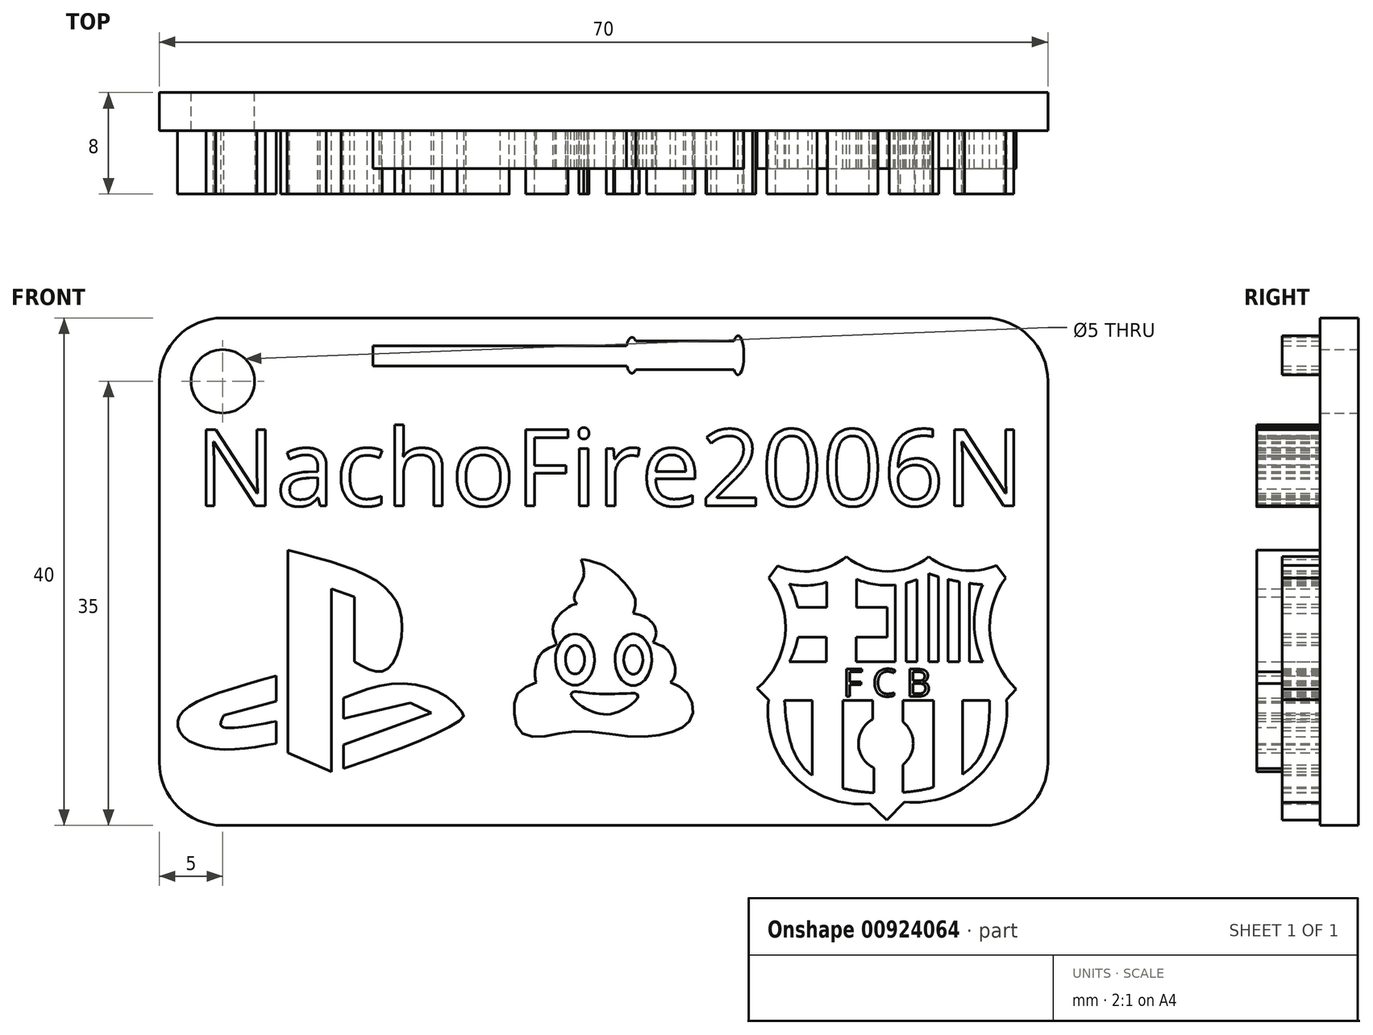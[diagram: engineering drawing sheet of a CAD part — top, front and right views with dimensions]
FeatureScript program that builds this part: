
annotation { "Feature Type Name" : "Feature", "Feature Type Description" : "" }
export const myFeature = defineFeature(function(context is Context, id is Id, definition is map)
    precondition{}
    {
        {
            var Q0;
            Q0=qCreatedBy(makeId("Front.planeOp"),FACE);
            var sketch = newSketch(context, id + "F0", { "sketchPlane" : qUnion([Q0])});
            skLineSegment(sketch, "E0.bottom", {"start": v(-5, 0) * mm, "end": v(-65, 0) * mm});
            skLineSegment(sketch, "E0.top", {"start": v(-5, 40) * mm, "end": v(-65, 40) * mm});
            skLineSegment(sketch, "E0.left", {"start": v(0, 5) * mm, "end": v(0, 35) * mm});
            skLineSegment(sketch, "E0.right", {"start": v(-70, 5) * mm, "end": v(-70, 35) * mm});
            skPoint(sketch, "E1.visualSharp", {"position": v(-70, 40) * mm});
            skArc(sketch, "E1.filletArc", {"start": v(-65, 40) * mm, "mid": v(-68.54, 38.54) * mm, "end": v(-70, 35) * mm});
            skPoint(sketch, "E2.visualSharp", {"position": v(-70, 0) * mm});
            skArc(sketch, "E2.filletArc", {"start": v(-70, 5) * mm, "mid": v(-68.54, 1.46) * mm, "end": v(-65, 0) * mm});
            skPoint(sketch, "E3.visualSharp", {"position": v(0, 40) * mm});
            skArc(sketch, "E3.filletArc", {"start": v(0, 35) * mm, "mid": v(-1.46, 38.54) * mm, "end": v(-5, 40) * mm});
            skPoint(sketch, "E4.visualSharp", {"position": v(0, 0) * mm});
            skArc(sketch, "E4.filletArc", {"start": v(-5, 0) * mm, "mid": v(-1.46, 1.46) * mm, "end": v(0, 5) * mm});
            skCircle(sketch, "E5", {"center": v(-65, 35) * mm, "radius": 2.5 * mm});
            skSolve(sketch);
        }
        {
            var Q0;
            Q0 = qSketchRegion(id + "F0", true);
            extrude(context, id + "F1", {"entities" : qUnion([Q0]), "depth" : 3 * mm, "offsetDistance" : 25 * mm});
        }
        {
            var Q0;
            Q0=makeQuery(id+"F1.opExtrude","CAP_FACE",FACE,{"disambiguationData":[OSD([sQuery(id+"F0.wireOp",EDGE,"E0.bottom"),sQuery(id+"F0.wireOp",EDGE,"E0.top"),sQuery(id+"F0.wireOp",EDGE,"E0.left"),sQuery(id+"F0.wireOp",EDGE,"E0.right"),sQuery(id+"F0.wireOp",EDGE,"E1.filletArc"),sQuery(id+"F0.wireOp",EDGE,"E2.filletArc"),sQuery(id+"F0.wireOp",EDGE,"E3.filletArc"),sQuery(id+"F0.wireOp",EDGE,"E4.filletArc"),sQuery(id+"F0.wireOp",EDGE,"E5")])],"isStart":false});
            var sketch = newSketch(context, id + "F2", { "sketchPlane" : qUnion([Q0])});
            skText(sketch, "E6", { "text": "NachoFire2006N", "fontName": "OpenSans-Regular.ttf"});
            skPoint(sketch, "E7.start.orphan", {"position": v(-58.07, 12.98) * mm});
            skPoint(sketch, "E8.start.orphan", {"position": v(-58.07, 12.23) * mm});
            skPoint(sketch, "E9.end.orphan", {"position": v(-55.4, 11.37) * mm});
            skPoint(sketch, "E10.start.orphan", {"position": v(-55.4, 12.32) * mm});
            skPoint(sketch, "E11.2.internal.orphan", {"position": v(-62.68, 9.55) * mm});
            skPoint(sketch, "E11.3.internal.orphan", {"position": v(-59.99, 9.94) * mm});
            skPoint(sketch, "E12.end.orphan", {"position": v(-62.68, 10.23) * mm});
            skPoint(sketch, "E13.end.orphan", {"position": v(-59.99, 10.93) * mm});
            skPoint(sketch, "E14.2.internal.orphan", {"position": v(-51.14, 11.2) * mm});
            skPoint(sketch, "E15.end.orphan", {"position": v(-56.52, 10.05) * mm});
            skPoint(sketch, "E15.start.orphan", {"position": v(-56.52, 11.2) * mm});
            skPoint(sketch, "E16.start.orphan", {"position": v(-56.52, 8.65) * mm});
            skLineSegment(sketch, "E17", {"start": v(-59.87, 21.7) * mm, "end": v(-59.87, 5.73) * mm});
            skLineSegment(sketch, "E18", {"start": v(-59.87, 5.73) * mm, "end": v(-56.44, 4.25) * mm});
            skLineSegment(sketch, "E19", {"start": v(-56.44, 4.25) * mm, "end": v(-56.44, 18.66) * mm});
            skLineSegment(sketch, "E20", {"start": v(-56.44, 18.66) * mm, "end": v(-54.63, 18) * mm});
            skLineSegment(sketch, "E21", {"start": v(-54.63, 18) * mm, "end": v(-54.63, 12.9) * mm});
            skFitSpline(sketch, "E22", {"points": [v(-59.87, 21.7) * mm, v(-52.24, 18.78) * mm, v(-50.89, 15.3) * mm, v(-52.24, 12.2) * mm, v(-54.63, 12.9) * mm], "startDerivative": vector(26.14, -6.65) * mm, "endDerivative": vector(-13.47, 7.9) * mm});
            skLineSegment(sketch, "E23", {"start": v(-55.5, 10.05) * mm, "end": v(-55.5, 8.43) * mm});
            skLineSegment(sketch, "E24", {"start": v(-55.5, 6.38) * mm, "end": v(-55.5, 4.5) * mm});
            skLineSegment(sketch, "E25", {"start": v(-55.5, 6.38) * mm, "end": v(-48.55, 8.86) * mm});
            skLineSegment(sketch, "E26", {"start": v(-48.55, 8.86) * mm, "end": v(-50.22, 9.67) * mm});
            skLineSegment(sketch, "E27", {"start": v(-50.22, 9.67) * mm, "end": v(-55.5, 8.43) * mm});
            skPoint(sketch, "E28.5.internal.snap0", {"position": v(-52.02, 7.62) * mm});
            skFitSpline(sketch, "E28", {"points": [v(-55.5, 10.05) * mm, v(-51.14, 11.2) * mm, v(-47.51, 10.24) * mm, v(-46.23, 9.03) * mm, v(-46.06, 8.54) * mm, v(-52.02, 5.69) * mm, v(-55.5, 4.5) * mm], "startDerivative": vector(21.53, 8.3) * mm, "endDerivative": vector(-15.4, -4.87) * mm});
            skLineSegment(sketch, "E29", {"start": v(-60.79, 11.8) * mm, "end": v(-60.79, 9.8) * mm});
            skLineSegment(sketch, "E30", {"start": v(-60.79, 8.2) * mm, "end": v(-60.79, 6.46) * mm});
            skLineSegment(sketch, "E31", {"start": v(-60.79, 9.8) * mm, "end": v(-64.91, 8.67) * mm});
            skFitSpline(sketch, "E32", {"points": [v(-64.91, 8.67) * mm, v(-65.16, 8.08) * mm, v(-65.02, 7.76) * mm, v(-60.79, 8.2) * mm], "startDerivative": vector(-1.43, -2.66) * mm, "endDerivative": vector(9.4, 1.72) * mm});
            skFitSpline(sketch, "E33", {"points": [v(-60.79, 6.46) * mm, v(-65.2, 6.01) * mm, v(-68.05, 6.95) * mm, v(-68.56, 8.16) * mm, v(-67.6, 9.4) * mm, v(-60.79, 11.8) * mm], "startDerivative": vector(-19.03, -3.5) * mm, "endDerivative": vector(27.45, 7.68) * mm});
            const initialGuessF2  = {"E6": [-0.06715, 0.0252, 1, 0, 0.00604]};
            skSetInitialGuess(sketch, initialGuessF2);
            skSolve(sketch);
        }
        {
            var Q0;
            Q0 = qSketchRegion(id + "F2", true);
            extrude(context, id + "F3", {"entities" : qUnion([Q0]), "operationType" : NewBodyOperationType.ADD, "depth" : 5 * mm, "offsetDistance" : 25 * mm});
        }
        {
            var Q0;
            {var subQ0=sQuery(id+"F0.wireOp",EDGE,"E0.left");var subQ1=sQuery(id+"F0.wireOp",EDGE,"E5");var subQ2=sQuery(id+"F0.wireOp",EDGE,"E4.filletArc");var subQ3=sQuery(id+"F0.wireOp",EDGE,"E3.filletArc");var subQ4=sQuery(id+"F0.wireOp",EDGE,"E2.filletArc");var subQ5=sQuery(id+"F0.wireOp",EDGE,"E1.filletArc");var subQ6=sQuery(id+"F0.wireOp",EDGE,"E0.bottom");var subQ7=sQuery(id+"F0.wireOp",EDGE,"E0.right");var subQ8=sQuery(id+"F0.wireOp",EDGE,"E0.top");Q0=makeQuery(id+"F3.boolean.opBoolean","SPLIT",FACE,{"disambiguationData":[TD([makeQuery(id+"F1.opExtrude","SWEPT_FACE",FACE,{"disambiguationData":[OSD([subQ6])]})])],"derivedFrom":makeQuery(id+"F1.opExtrude","CAP_FACE",FACE,{"disambiguationData":[OSD([subQ6,subQ8,subQ0,subQ7,subQ5,subQ4,subQ3,subQ2,subQ1])],"isStart":false})});}
            var sketch = newSketch(context, id + "F4", { "sketchPlane" : qUnion([Q0])});
            skCircle(sketch, "E34", {"center": v(-12.76, 6.47) * mm, "radius": 2.16 * mm});
            skLineSegment(sketch, "E35", {"start": v(-20.76, 9.86) * mm, "end": v(-4.58, 9.86) * mm});
            skLineSegment(sketch, "E36", {"start": v(-20.37, 12.9) * mm, "end": v(-5.13, 12.9) * mm});
            skFitSpline(sketch, "E37", {"points": [v(-20.76, 9.86) * mm, v(-18.77, 4.11) * mm, v(-9.71, 2.84) * mm, v(-5.3, 5.55) * mm, v(-4.58, 9.86) * mm], "startDerivative": vector(2.2, -26.55) * mm, "endDerivative": vector(0.34, 21.86) * mm});
            skLineSegment(sketch, "E38", {"start": v(-18.55, 9.86) * mm, "end": v(-18.55, 3.95) * mm});
            skLineSegment(sketch, "E39", {"start": v(-16.15, 2.93) * mm, "end": v(-16.15, 9.86) * mm});
            skLineSegment(sketch, "E40", {"start": v(-13.8, 9.86) * mm, "end": v(-13.8, 8.37) * mm});
            skLineSegment(sketch, "E41", {"start": v(-13.7, 4.53) * mm, "end": v(-13.7, 2.58) * mm});
            skLineSegment(sketch, "E42", {"start": v(-11.42, 9.86) * mm, "end": v(-11.42, 8.16) * mm});
            skLineSegment(sketch, "E43", {"start": v(-11.43, 4.77) * mm, "end": v(-11.43, 2.6) * mm});
            skLineSegment(sketch, "E44", {"start": v(-9, 3.01) * mm, "end": v(-9, 9.86) * mm});
            skLineSegment(sketch, "E45", {"start": v(-6.73, 9.86) * mm, "end": v(-6.73, 4.01) * mm});
            skArc(sketch, "E46", {"start": v(-20.37, 12.9) * mm, "mid": v(-19.59, 15.96) * mm, "end": v(-20.37, 19.02) * mm});
            skArc(sketch, "E47", {"start": v(-5.13, 18.98) * mm, "mid": v(-5.8, 15.93) * mm, "end": v(-5.13, 12.9) * mm});
            skArc(sketch, "E48", {"start": v(-9.38, 19.85) * mm, "mid": v(-7.29, 19.27) * mm, "end": v(-5.13, 18.98) * mm});
            skArc(sketch, "E49", {"start": v(-15.95, 19.85) * mm, "mid": v(-12.67, 18.92) * mm, "end": v(-9.38, 19.85) * mm});
            skArc(sketch, "E50", {"start": v(-20.37, 19.02) * mm, "mid": v(-18.08, 19.01) * mm, "end": v(-15.95, 19.85) * mm});
            skLineSegment(sketch, "E51", {"start": v(-12.67, 18.92) * mm, "end": v(-12.67, 12.9) * mm});
            skLineSegment(sketch, "E52", {"start": v(-12.02, 12.9) * mm, "end": v(-12.02, 18.96) * mm});
            skLineSegment(sketch, "E53", {"start": v(-11.17, 19.1) * mm, "end": v(-11.17, 12.9) * mm});
            skLineSegment(sketch, "E54", {"start": v(-10.31, 19.38) * mm, "end": v(-10.31, 12.9) * mm});
            skLineSegment(sketch, "E55", {"start": v(-9.38, 19.85) * mm, "end": v(-9.38, 12.9) * mm});
            skLineSegment(sketch, "E56", {"start": v(-8.62, 19.6) * mm, "end": v(-8.62, 12.9) * mm});
            skLineSegment(sketch, "E57", {"start": v(-7.87, 19.4) * mm, "end": v(-7.87, 12.9) * mm});
            skLineSegment(sketch, "E58", {"start": v(-6.96, 19.2) * mm, "end": v(-6.96, 12.9) * mm});
            skLineSegment(sketch, "E59", {"start": v(-6.2, 19.09) * mm, "end": v(-6.2, 12.9) * mm});
            skLineSegment(sketch, "E60", {"start": v(-15.08, 19.4) * mm, "end": v(-15.08, 17.2) * mm});
            skLineSegment(sketch, "E61", {"start": v(-15.08, 17.2) * mm, "end": v(-12.67, 17.2) * mm});
            skLineSegment(sketch, "E62", {"start": v(-12.67, 14.85) * mm, "end": v(-15.1, 14.85) * mm});
            skLineSegment(sketch, "E63", {"start": v(-15.1, 14.85) * mm, "end": v(-15.1, 12.9) * mm});
            skLineSegment(sketch, "E64", {"start": v(-17.42, 19.18) * mm, "end": v(-17.42, 17.2) * mm});
            skLineSegment(sketch, "E65", {"start": v(-17.42, 17.2) * mm, "end": v(-19.7, 17.2) * mm});
            skLineSegment(sketch, "E66", {"start": v(-17.45, 14.85) * mm, "end": v(-19.68, 14.85) * mm});
            skLineSegment(sketch, "E67", {"start": v(-17.45, 14.85) * mm, "end": v(-17.45, 12.9) * mm});
            skText(sketch, "E68", { "text": "F C B", "fontName": "OpenSans-Regular.ttf"});
            skLineSegment(sketch, "E69", {"start": v(-4.05, 20.5) * mm, "end": v(-3.33, 19.52) * mm});
            skLineSegment(sketch, "E70", {"start": v(-22, 19.52) * mm, "end": v(-21.28, 20.47) * mm});
            skLineSegment(sketch, "E71", {"start": v(-22.91, 10.8) * mm, "end": v(-22, 9.88) * mm});
            skLineSegment(sketch, "E72", {"start": v(-2.5, 10.76) * mm, "end": v(-3.26, 9.92) * mm});
            skPoint(sketch, "E72.startSnap0", {"position": v(-1.83, 10.76) * mm});
            skLineSegment(sketch, "E73", {"start": v(-14.05, 1.73) * mm, "end": v(-12.68, 0.4) * mm});
            skLineSegment(sketch, "E74", {"start": v(-12.68, 0.4) * mm, "end": v(-11.3, 1.85) * mm});
            skArc(sketch, "E75", {"start": v(-22, 9.88) * mm, "mid": v(-19.99, 3.89) * mm, "end": v(-14.05, 1.73) * mm});
            skArc(sketch, "E76", {"start": v(-11.3, 1.85) * mm, "mid": v(-5.36, 3.98) * mm, "end": v(-3.26, 9.92) * mm});
            skArc(sketch, "E77", {"start": v(-3.33, 19.52) * mm, "mid": v(-4.55, 14.98) * mm, "end": v(-2.5, 10.76) * mm});
            skPoint(sketch, "E78", {"position": v(-15.87, 21.19) * mm});
            skPoint(sketch, "E79", {"position": v(-9.38, 21.19) * mm});
            skArc(sketch, "E80", {"start": v(-22.91, 10.8) * mm, "mid": v(-20.7, 14.97) * mm, "end": v(-22, 19.52) * mm});
            skArc(sketch, "E81", {"start": v(-21.28, 20.47) * mm, "mid": v(-18.47, 20.06) * mm, "end": v(-15.87, 21.19) * mm});
            skArc(sketch, "E82", {"start": v(-15.87, 21.19) * mm, "mid": v(-12.63, 20.02) * mm, "end": v(-9.38, 21.19) * mm});
            skArc(sketch, "E83", {"start": v(-9.38, 21.19) * mm, "mid": v(-6.81, 20.11) * mm, "end": v(-4.05, 20.5) * mm});
            skFitSpline(sketch, "E84", {"points": [v(-12.76, 6.47) * mm, v(-13, 5.98) * mm, v(-13.7, 5.93) * mm, v(-14.18, 6.95) * mm, v(-13.92, 8.3) * mm], "startDerivative": vector(-0.68, -2.87) * mm, "endDerivative": vector(1.41, 4.28) * mm});
            skFitSpline(sketch, "E85", {"points": [v(-12.76, 6.47) * mm, v(-13, 7.36) * mm, v(-12.35, 7.64) * mm, v(-10.62, 6.7) * mm], "startDerivative": vector(-1.62, 3.35) * mm, "endDerivative": vector(4.18, -3.07) * mm});
            skArc(sketch, "E86", {"start": v(-12.76, 8.63) * mm, "mid": v(-12.98, 8.1) * mm, "end": v(-12.68, 7.62) * mm});
            skFitSpline(sketch, "E87", {"points": [v(-12.76, 6.47) * mm, v(-12, 6.47) * mm, v(-11.62, 5.83) * mm, v(-12.93, 4.77) * mm, v(-13.96, 4.68) * mm], "startDerivative": vector(3.7, 0.74) * mm, "endDerivative": vector(-3.72, 0.32) * mm});
            skArc(sketch, "E88", {"start": v(-10.8, 5.6) * mm, "mid": v(-11.15, 5.91) * mm, "end": v(-11.62, 5.83) * mm});
            skArc(sketch, "E89", {"start": v(-14.68, 5.48) * mm, "mid": v(-14.11, 5.54) * mm, "end": v(-13.7, 5.93) * mm});
            const initialGuessF4  = {"E68": [-0.01616, 0.01018, 1, 0, 0.00216]};
            skSetInitialGuess(sketch, initialGuessF4);
            skSolve(sketch);
        }
        {
            var Q0;
            Q0 = qSketchRegion(id + "F4", true);
            var Q1;
            {var subQ4=sQuery(id+"F4.wireOp",EDGE,"E60");Q1=makeQuery(id+"F4.imprint","IMPRINT",FACE,{"disambiguationData":[TD([[makeQuery(id+"F4.imprint","IMPRINT",EDGE,{"derivedFrom":subQ4}),-1.0]])]});}
            var Q2;
            {var subQ0=sQuery(id+"F4.wireOp",EDGE,"E58");Q2=makeQuery(id+"F4.imprint","IMPRINT",FACE,{"disambiguationData":[TD([[makeQuery(id+"F4.imprint","IMPRINT",EDGE,{"derivedFrom":subQ0}),1.0]])]});}
            var Q3;
            {var subQ0=sQuery(id+"F4.wireOp",EDGE,"E56");Q3=makeQuery(id+"F4.imprint","IMPRINT",FACE,{"disambiguationData":[TD([[makeQuery(id+"F4.imprint","IMPRINT",EDGE,{"derivedFrom":subQ0}),1.0]])]});}
            var Q4;
            {var subQ0=sQuery(id+"F4.wireOp",EDGE,"E54");Q4=makeQuery(id+"F4.imprint","IMPRINT",FACE,{"disambiguationData":[TD([[makeQuery(id+"F4.imprint","IMPRINT",EDGE,{"derivedFrom":subQ0}),1.0]])]});}
            var Q5;
            {var subQ0=sQuery(id+"F4.wireOp",EDGE,"E52");Q5=makeQuery(id+"F4.imprint","IMPRINT",FACE,{"disambiguationData":[TD([[makeQuery(id+"F4.imprint","IMPRINT",EDGE,{"derivedFrom":subQ0}),-1.0]])]});}
            var Q6;
            {var subQ0=sQuery(id+"F4.wireOp",EDGE,"E34");var subQ1=makeQuery(id+"F4.imprint","INTERSECT",VERTEX,{"derivedFrom":[subQ0,sQuery(id+"F4.wireOp",EDGE,"E40")]});Q6=makeQuery(id+"F4.imprint","IMPRINT",FACE,{"disambiguationData":[TD([[makeQuery(id+"F4.imprint","IMPRINT",EDGE,{"disambiguationData":[TD([[subQ1,1.0]])],"derivedFrom":subQ0}),1.0]])]});}
            var Q7;
            {var subQ0=sQuery(id+"F4.wireOp",EDGE,"E40");Q7=makeQuery(id+"F4.imprint","IMPRINT",FACE,{"disambiguationData":[TD([[makeQuery(id+"F4.imprint","IMPRINT",EDGE,{"derivedFrom":subQ0}),1.0]])]});}
            var Q8;
            {var subQ0=sQuery(id+"F4.wireOp",EDGE,"E38");Q8=makeQuery(id+"F4.imprint","IMPRINT",FACE,{"disambiguationData":[TD([[makeQuery(id+"F4.imprint","IMPRINT",EDGE,{"derivedFrom":subQ0}),1.0]])]});}
            var Q9;
            {var subQ0=sQuery(id+"F4.wireOp",EDGE,"E41");Q9=makeQuery(id+"F4.imprint","IMPRINT",FACE,{"disambiguationData":[TD([[makeQuery(id+"F4.imprint","IMPRINT",EDGE,{"derivedFrom":subQ0}),1.0]])]});}
            var Q10;
            {var subQ0=sQuery(id+"F4.wireOp",EDGE,"E44");Q10=makeQuery(id+"F4.imprint","IMPRINT",FACE,{"disambiguationData":[TD([[makeQuery(id+"F4.imprint","IMPRINT",EDGE,{"derivedFrom":subQ0}),-1.0]])]});}
            var Q11;
            Q11=makeQuery(id+"F4.imprint","IMPRINT",FACE,{"disambiguationData":[TD([[makeQuery(id+"F4.imprint","IMPRINT",EDGE,{"derivedFrom":sQuery(id+"F4.wireOp",EDGE,"E68.sketch_text.stroke-36")}),1.0]])]});
            var Q12;
            Q12=makeQuery(id+"F4.imprint","IMPRINT",FACE,{"disambiguationData":[TD([[makeQuery(id+"F4.imprint","IMPRINT",EDGE,{"derivedFrom":sQuery(id+"F4.wireOp",EDGE,"E68.sketch_text.stroke-43")}),1.0]])]});
            var Q13;
            {var subQ3=sQuery(id+"F4.wireOp",EDGE,"E88");Q13=makeQuery(id+"F4.imprint","IMPRINT",FACE,{"disambiguationData":[TD([[makeQuery(id+"F4.imprint","IMPRINT",EDGE,{"derivedFrom":subQ3}),-1.0]])]});}
            var Q14;
            {var subQ3=sQuery(id+"F4.wireOp",EDGE,"E88");Q14=makeQuery(id+"F4.imprint","IMPRINT",FACE,{"disambiguationData":[TD([[makeQuery(id+"F4.imprint","IMPRINT",EDGE,{"derivedFrom":subQ3}),1.0]])]});}
            var Q15;
            {var subQ3=sQuery(id+"F4.wireOp",EDGE,"E89");Q15=makeQuery(id+"F4.imprint","IMPRINT",FACE,{"disambiguationData":[TD([[makeQuery(id+"F4.imprint","IMPRINT",EDGE,{"derivedFrom":subQ3}),1.0]])]});}
            var Q16;
            {var subQ6=sQuery(id+"F4.wireOp",EDGE,"E89");Q16=makeQuery(id+"F4.imprint","IMPRINT",FACE,{"disambiguationData":[TD([[makeQuery(id+"F4.imprint","IMPRINT",EDGE,{"derivedFrom":subQ6}),-1.0]])]});}
            var Q17;
            {var subQ4=sQuery(id+"F4.wireOp",EDGE,"E86");Q17=makeQuery(id+"F4.imprint","IMPRINT",FACE,{"disambiguationData":[TD([[makeQuery(id+"F4.imprint","IMPRINT",EDGE,{"derivedFrom":subQ4}),1.0]])]});}
            extrude(context, id + "F5", {"entities" : qUnion([Q0, Q1, Q2, Q3, Q4, Q5, Q6, Q7, Q8, Q9, Q10, Q11, Q12, Q13, Q14, Q15, Q16, Q17]), "operationType" : NewBodyOperationType.ADD, "depth" : 3 * mm, "offsetDistance" : 25 * mm});
        }
        {
            var Q0;
            {var subQ94=sQuery(id+"F0.wireOp",EDGE,"E0.left");var subQ100=sQuery(id+"F0.wireOp",EDGE,"E5");var subQ107=sQuery(id+"F0.wireOp",EDGE,"E4.filletArc");var subQ114=sQuery(id+"F0.wireOp",EDGE,"E3.filletArc");var subQ120=sQuery(id+"F0.wireOp",EDGE,"E2.filletArc");var subQ128=sQuery(id+"F0.wireOp",EDGE,"E1.filletArc");var subQ131=sQuery(id+"F0.wireOp",EDGE,"E0.bottom");var subQ132=makeQuery(id+"F1.opExtrude","SWEPT_FACE",FACE,{"disambiguationData":[OSD([subQ131])]});var subQ136=sQuery(id+"F0.wireOp",EDGE,"E0.right");var subQ140=sQuery(id+"F0.wireOp",EDGE,"E0.top");Q0=makeQuery(id+"F5.boolean.opBoolean","SPLIT",FACE,{"disambiguationData":[TD([subQ132])],"derivedFrom":makeQuery(id+"F3.boolean.opBoolean","SPLIT",FACE,{"disambiguationData":[TD([subQ132])],"derivedFrom":makeQuery(id+"F1.opExtrude","CAP_FACE",FACE,{"disambiguationData":[OSD([subQ131,subQ140,subQ94,subQ136,subQ128,subQ120,subQ114,subQ107,subQ100])],"isStart":false})})});}
            var sketch = newSketch(context, id + "F6", { "sketchPlane" : qUnion([Q0])});
            skLineSegment(sketch, "E90", {"start": v(-32.18, 35.9) * mm, "end": v(-24.8, 35.9) * mm});
            skLineSegment(sketch, "E91", {"start": v(-32.18, 38.2) * mm, "end": v(-24.8, 38.2) * mm});
            skEllipse(sketch, "E92", {"center": v(-24.4, 37.05) * mm, "majorRadius": 1.55 * mm, "minorRadius": 0.46 * mm, "majorAxis": v(0, 1)});
            skLineSegment(sketch, "E93", {"start": v(-24.8, 38.2) * mm, "end": v(-24.72, 38.2) * mm});
            skLineSegment(sketch, "E94", {"start": v(-24.8, 35.9) * mm, "end": v(-24.72, 35.9) * mm});
            skEllipse(sketch, "E95", {"center": v(-32.77, 37.05) * mm, "majorRadius": 1.43 * mm, "minorRadius": 0.49 * mm, "majorAxis": v(0, 1)});
            skLineSegment(sketch, "E96", {"start": v(-32.18, 38.2) * mm, "end": v(-32.48, 38.2) * mm});
            skLineSegment(sketch, "E97", {"start": v(-32.18, 35.9) * mm, "end": v(-32.48, 35.9) * mm});
            skLineSegment(sketch, "E98", {"start": v(-33.18, 37.8) * mm, "end": v(-53.18, 37.8) * mm});
            skLineSegment(sketch, "E99", {"start": v(-53.18, 37.8) * mm, "end": v(-53.18, 36.2) * mm});
            skLineSegment(sketch, "E100", {"start": v(-53.18, 36.2) * mm, "end": v(-33.16, 36.2) * mm});
            skSolve(sketch);
        }
        {
            var Q0;
            {var subQ0=sQuery(id+"F6.wireOp",EDGE,"E92");var subQ1=makeQuery(id+"F6.imprint","INTERSECT",VERTEX,{"derivedFrom":[subQ0,sQuery(id+"F6.wireOp",EDGE,"E93")]});Q0=makeQuery(id+"F6.imprint","IMPRINT",FACE,{"disambiguationData":[TD([[makeQuery(id+"F6.imprint","IMPRINT",EDGE,{"disambiguationData":[TD([[subQ1,-1.0]])],"derivedFrom":subQ0}),1.0]])]});}
            var Q1;
            {var subQ0=sQuery(id+"F6.wireOp",EDGE,"E98");Q1=makeQuery(id+"F6.imprint","IMPRINT",FACE,{"disambiguationData":[TD([[makeQuery(id+"F6.imprint","IMPRINT",EDGE,{"derivedFrom":subQ0}),1.0]])]});}
            var Q2;
            {var subQ0=sQuery(id+"F6.wireOp",EDGE,"uE8yDqcb-mppc-h1kh-nOKK-Aj263YFdmIPn");Q2=makeQuery(id+"F6.imprint","IMPRINT",FACE,{"disambiguationData":[TD([[makeQuery(id+"F6.imprint","IMPRINT",EDGE,{"derivedFrom":subQ0}),-1.0]])]});}
            var Q3;
            {var subQ0=sQuery(id+"F6.wireOp",EDGE,"E93");Q3=makeQuery(id+"F6.imprint","IMPRINT",FACE,{"disambiguationData":[TD([[makeQuery(id+"F6.imprint","IMPRINT",EDGE,{"derivedFrom":subQ0}),-1.0]])]});}
            var Q4;
            {var subQ0=sQuery(id+"F6.wireOp",EDGE,"E95");var subQ1=makeQuery(id+"F6.imprint","INTERSECT",VERTEX,{"derivedFrom":[subQ0,sQuery(id+"F6.wireOp",EDGE,"E98")]});Q4=makeQuery(id+"F6.imprint","IMPRINT",FACE,{"disambiguationData":[TD([[makeQuery(id+"F6.imprint","IMPRINT",EDGE,{"disambiguationData":[TD([[subQ1,-1.0]])],"derivedFrom":subQ0}),1.0]])]});}
            var Q5;
            {var subQ0=sQuery(id+"F6.wireOp",EDGE,"E96");Q5=makeQuery(id+"F6.imprint","IMPRINT",FACE,{"disambiguationData":[TD([[makeQuery(id+"F6.imprint","IMPRINT",EDGE,{"derivedFrom":subQ0}),1.0]])]});}
            extrude(context, id + "F7", {"entities" : qUnion([Q0, Q1, Q2, Q3, Q4, Q5]), "operationType" : NewBodyOperationType.ADD, "depth" : 3 * mm, "offsetDistance" : 25 * mm});
        }
        {
            var Q0;
            {var subQ94=sQuery(id+"F0.wireOp",EDGE,"E0.left");var subQ100=sQuery(id+"F0.wireOp",EDGE,"E5");var subQ107=sQuery(id+"F0.wireOp",EDGE,"E4.filletArc");var subQ114=sQuery(id+"F0.wireOp",EDGE,"E3.filletArc");var subQ120=sQuery(id+"F0.wireOp",EDGE,"E2.filletArc");var subQ128=sQuery(id+"F0.wireOp",EDGE,"E1.filletArc");var subQ131=sQuery(id+"F0.wireOp",EDGE,"E0.bottom");var subQ132=makeQuery(id+"F1.opExtrude","SWEPT_FACE",FACE,{"disambiguationData":[OSD([subQ131])]});var subQ136=sQuery(id+"F0.wireOp",EDGE,"E0.right");var subQ140=sQuery(id+"F0.wireOp",EDGE,"E0.top");Q0=makeQuery(id+"F5.boolean.opBoolean","SPLIT",FACE,{"disambiguationData":[TD([subQ132])],"derivedFrom":makeQuery(id+"F3.boolean.opBoolean","SPLIT",FACE,{"disambiguationData":[TD([subQ132])],"derivedFrom":makeQuery(id+"F1.opExtrude","CAP_FACE",FACE,{"disambiguationData":[OSD([subQ131,subQ140,subQ94,subQ136,subQ128,subQ120,subQ114,subQ107,subQ100])],"isStart":false})})});}
            var sketch = newSketch(context, id + "F8", { "sketchPlane" : qUnion([Q0])});
            skFitSpline(sketch, "E101", {"points": [v(-36.76, 20.98) * mm, v(-34.76, 20.36) * mm, v(-33.11, 18.82) * mm, v(-32.5, 17.74) * mm, v(-32.65, 16.71) * mm], "startDerivative": vector(7.28, -1.32) * mm, "endDerivative": vector(-1.54, -5.24) * mm});
            skFitSpline(sketch, "E102", {"points": [v(-32.65, 16.71) * mm, v(-31.6, 16.35) * mm, v(-30.88, 15.36) * mm, v(-31.09, 14.41) * mm], "startDerivative": vector(3.26, -0.64) * mm, "endDerivative": vector(-1.3, -2.96) * mm});
            skFitSpline(sketch, "E103", {"points": [v(-31.09, 14.41) * mm, v(-30.06, 13.92) * mm, v(-29.49, 12.96) * mm, v(-29.39, 11.82) * mm, v(-29.74, 11.27) * mm], "startDerivative": vector(4.22, -1.47) * mm, "endDerivative": vector(-2.13, -2.35) * mm});
            skFitSpline(sketch, "E104", {"points": [v(-29.74, 11.27) * mm, v(-28.54, 10.57) * mm, v(-27.95, 9.13) * mm, v(-28.34, 8.08) * mm, v(-29.6, 7.39) * mm, v(-32.65, 6.99) * mm, v(-37, 7.44) * mm, v(-40.04, 6.99) * mm, v(-41.59, 7.44) * mm, v(-42.03, 8.98) * mm, v(-41.73, 10.42) * mm, v(-40.3, 11.27) * mm], "startDerivative": vector(16.9, -6.74) * mm, "endDerivative": vector(20.33, 8) * mm});
            skFitSpline(sketch, "E105", {"points": [v(-40.3, 11.27) * mm, v(-40.41, 11.8) * mm, v(-40.3, 12.75) * mm, v(-39.83, 13.64) * mm, v(-38.7, 14.24) * mm], "startDerivative": vector(-0.83, 2.56) * mm, "endDerivative": vector(4.33, 1.69) * mm});
            skFitSpline(sketch, "E106", {"points": [v(-38.7, 14.24) * mm, v(-39, 15.32) * mm, v(-38.7, 16.3) * mm, v(-37.61, 17.3) * mm, v(-37.1, 17.46) * mm], "startDerivative": vector(-1.5, 4.15) * mm, "endDerivative": vector(2.5, 0.45) * mm});
            skFitSpline(sketch, "E107", {"points": [v(-37.1, 17.46) * mm, v(-37.32, 18.03) * mm, v(-36.69, 19.31) * mm, v(-36.55, 20.1) * mm, v(-36.76, 20.98) * mm], "startDerivative": vector(-1.77, 2.47) * mm, "endDerivative": vector(-1.07, 3.66) * mm});
            skEllipse(sketch, "E108", {"center": v(-37.25, 13.07) * mm, "majorRadius": 2.02 * mm, "minorRadius": 1.55 * mm, "majorAxis": v(0, 1)});
            skEllipse(sketch, "E109", {"center": v(-37.25, 13.07) * mm, "majorRadius": 1.13 * mm, "minorRadius": 0.75 * mm, "majorAxis": v(0, 1)});
            skEllipse(sketch, "E110", {"center": v(-32.66, 13.07) * mm, "majorRadius": 1.15 * mm, "minorRadius": 0.75 * mm, "majorAxis": v(0, 1)});
            skEllipse(sketch, "E111", {"center": v(-32.66, 13.07) * mm, "majorRadius": 2.05 * mm, "minorRadius": 1.45 * mm, "majorAxis": v(0, 1)});
            skFitSpline(sketch, "E112", {"points": [v(-37.58, 10.28) * mm, v(-37.03, 9.63) * mm, v(-36.01, 9.02) * mm, v(-34.81, 8.75) * mm, v(-33.44, 9.15) * mm, v(-32.29, 10.15) * mm, v(-32.5, 10.43) * mm], "startDerivative": vector(3.16, -4.5) * mm, "endDerivative": vector(-3.6, 2.44) * mm});
            skFitSpline(sketch, "E113", {"points": [v(-37.58, 10.28) * mm, v(-37.42, 10.52) * mm, v(-36.25, 10.43) * mm, v(-32.5, 10.43) * mm], "startDerivative": vector(0.65, 1.93) * mm, "endDerivative": vector(7.6, 0.31) * mm});
            skSolve(sketch);
        }
        {
            var Q0;
            Q0 = qSketchRegion(id + "F8", true);
            var Q1;
            Q1=makeQuery(id+"F8.imprint","IMPRINT",FACE,{"disambiguationData":[TD([[makeQuery(id+"F8.imprint","IMPRINT",EDGE,{"derivedFrom":sQuery(id+"F8.wireOp",EDGE,"E109")}),1.0]])]});
            var Q2;
            Q2=makeQuery(id+"F8.imprint","IMPRINT",FACE,{"disambiguationData":[TD([[makeQuery(id+"F8.imprint","IMPRINT",EDGE,{"derivedFrom":sQuery(id+"F8.wireOp",EDGE,"E110")}),1.0]])]});
            extrude(context, id + "F9", {"entities" : qUnion([Q0, Q1, Q2]), "operationType" : NewBodyOperationType.ADD, "depth" : 3 * mm, "offsetDistance" : 25 * mm});
        }
    });
